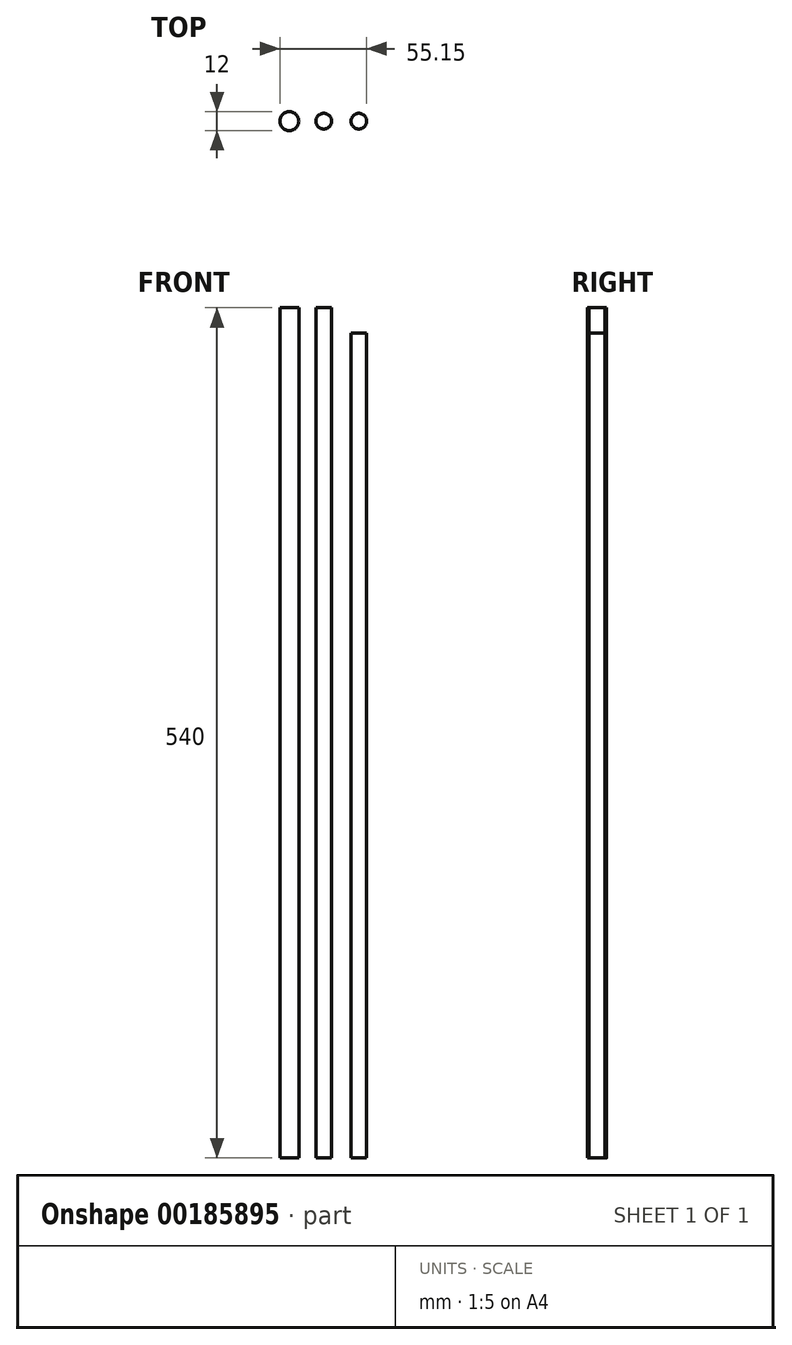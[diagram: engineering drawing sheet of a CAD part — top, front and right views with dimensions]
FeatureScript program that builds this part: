
annotation { "Feature Type Name" : "Feature", "Feature Type Description" : "" }
export const myFeature = defineFeature(function(context is Context, id is Id, definition is map)
    precondition{}
    {
        {
            var Q0;
            Q0=qCreatedBy(makeId("Top.planeOp"),FACE);
            var sketch = newSketch(context, id + "F0", { "sketchPlane" : qUnion([Q0])});
            skCircle(sketch, "E0", {"center": v(0, 0) * mm, "radius": 5 * mm});
            skSolve(sketch);
        }
        {
            var Q0;
            Q0=qSketchRegion(id+"F0",true);
            extrude(context, id + "F1", {"entities" : qUnion([Q0]), "depth" : 540 * mm});
        }
        {
            var Q0;
            Q0=qCreatedBy(makeId("Top.planeOp"),FACE);
            var sketch = newSketch(context, id + "F2", { "sketchPlane" : qUnion([Q0])});
            skCircle(sketch, "E1", {"center": v(22.28, 0) * mm, "radius": 5 * mm});
            skSolve(sketch);
        }
        {
            var Q0;
            Q0 = qSketchRegion(id + "F2", true);
            extrude(context, id + "F3", {"entities" : qUnion([Q0]), "depth" : 524 * mm});
        }
        {
            var Q0;
            Q0=qCreatedBy(makeId("Top.planeOp"),FACE);
            var sketch = newSketch(context, id + "F4", { "sketchPlane" : qUnion([Q0])});
            skCircle(sketch, "E2", {"center": v(-21.87, 0) * mm, "radius": 6 * mm});
            skSolve(sketch);
        }
        {
            var Q0;
            Q0 = qSketchRegion(id + "F4", true);
            extrude(context, id + "F5", {"entities" : qUnion([Q0]), "depth" : 540 * mm});
        }
    });
